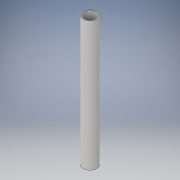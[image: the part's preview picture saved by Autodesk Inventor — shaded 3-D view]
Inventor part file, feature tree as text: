
AUTODESK INVENTOR PART (.ipt)
format: ipt  version: 2017 (Build 210142000, 142)  size: 93,184 bytes
history: native  units: in
note: dims shown in document units (in); Inventor stores cm internally (conversion verified against a paired STEP export)
features: extrude x1, sketch x1
ambient origin geometry x8: Origin, YZ Plane, XZ Plane, XY Plane, X Axis, Y Axis, Z Axis, Center Point
bodies: Body1 (feature_tree)
feature tree (2):
  extrude  "Extrusion2"  Depth=10.0in
  sketch  "Sketch1"  dims[d0=1.06in d1=0.914in d4=10.0in d5=0.0in]
